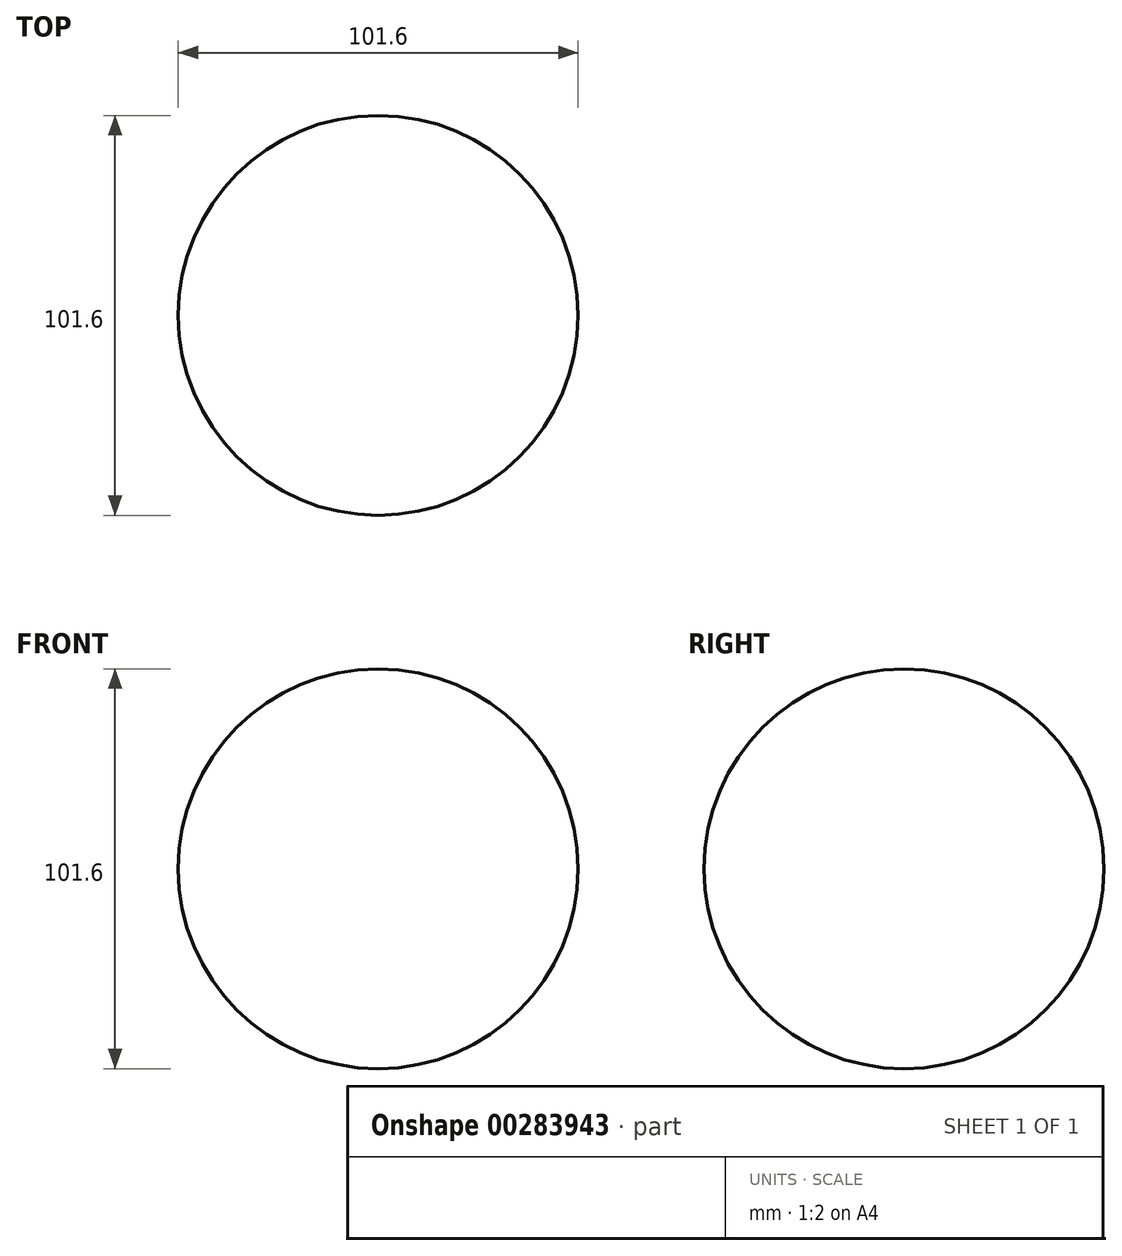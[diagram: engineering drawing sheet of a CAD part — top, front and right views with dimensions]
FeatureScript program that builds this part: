
annotation { "Feature Type Name" : "Feature", "Feature Type Description" : "" }
export const myFeature = defineFeature(function(context is Context, id is Id, definition is map)
    precondition{}
    {
        {
            var Q0;
            Q0=qCreatedBy(makeId("Front.planeOp"),FACE);
            var sketch = newSketch(context, id + "F0", { "sketchPlane" : qUnion([Q0])});
            skArc(sketch, "E0", {"start": v(0, -50.8) * mm, "mid": v(50.8, 0) * mm, "end": v(0, 50.8) * mm});
            skLineSegment(sketch, "E1", {"start": v(0, 50.8) * mm, "end": v(0, -50.8) * mm});
            skSolve(sketch);
        }
        {
            var Q0;
            Q0=makeQuery(id+"F0.imprint","IMPRINT",FACE,{"disambiguationData":[TD([[makeQuery(id+"F0.imprint","IMPRINT",EDGE,{"derivedFrom":sQuery(id+"F0.wireOp",EDGE,"E0")}),1.0]])]});
            var Q1;
            Q1=sQuery(id+"F0.wireOp",EDGE,"E1");
            revolve(context, id + "F1", {"entities" : qUnion([Q0]), "axis" : qUnion([Q1]), "revolveType" : RevolveType.FULL});
        }
    });
